# Revit family: Sanitary_Accessories_AXOR_42870XXX-AXOR-Universal-Softsquare-Adapt_NEW
name_source: partatom
category: Furniture
revit_build: Autodesk Revit 2018 (Build: 20170223_1515(x64)
units: mm (PartAtom-declared; Revit-internal decimal feet)

## family parameters
Always vertical = No
Cut with Voids When Loaded = No
OmniClass Number = 23.31.25.00
OmniClass Title = Toilet and Bath Specialties
Room Calculation Point = No
Shared = No
Work Plane-Based = Yes

## types (1)
- Default - please load Revit Family Type Catalog
    Always visible = Yes
    BIMobject category = Accessories
    Default Elevation = 1219.2 mm  [stored 4 ft]
    Description = AXOR Universal Softsquare Adapter set
    Design country = Germany
    EAN code = 4059625428375
    Edition number = 1
    GTIN code = https://4059625428375
    IFC Classification = Furnishing Element
    Manufacturer = AXOR
    Manufacturer country = Germany
    Manufacturer name = AXOR
    Material 1 = AXOR - Plastic - Gray
    Material 2 = AXOR - Metal - 000 Chrome
    Material secondary = Chrome
    Model = 42870XXX
    OmniClass Code = 23-31 25 00
    OmniClass Description = Toilet and Bath Specialties
    Product Guid = 88e86316-f1c3-48f3-a7ee-bb112e0cd6ac
    Product SKU = 42870XXX
    Product data url = https://bimobject.com
    Product family = AXOR Universal Softsquare
    Product group = Adapter sets
    Product name = 42870XXX AXOR Universal Softsquare Adapter set
    QR code = https://bimobject.com
    URL = https://www.axor-design.com
    Weight Net (Kg) = 90

note: [stored X ft] marks values corroborated as IEEE doubles in the binary element streams (Revit-internal decimal feet)
